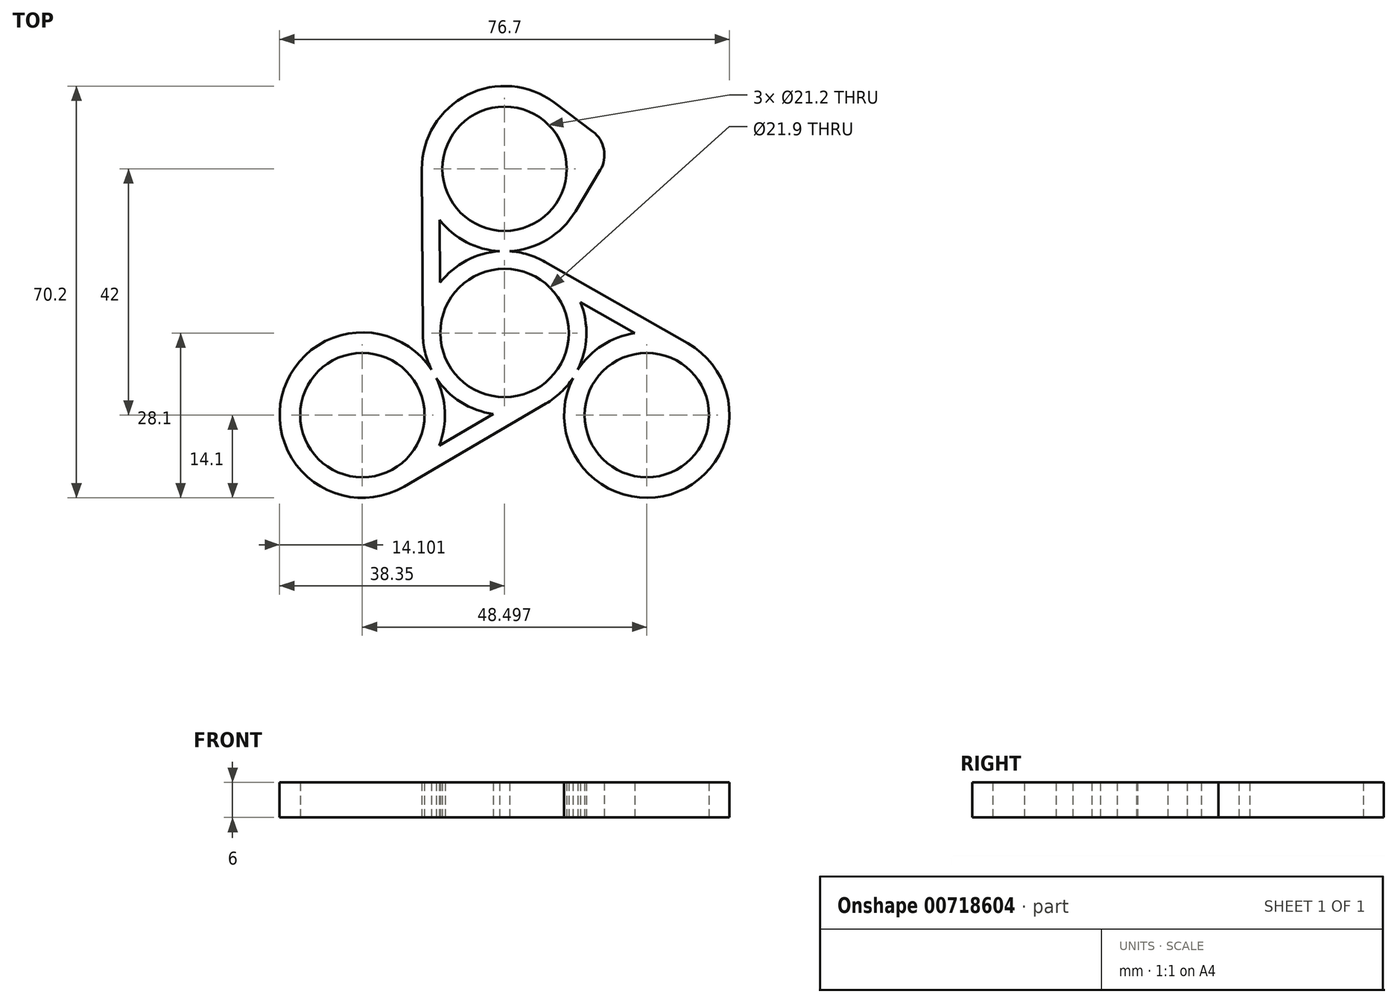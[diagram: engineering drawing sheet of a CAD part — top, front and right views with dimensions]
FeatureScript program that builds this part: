
annotation { "Feature Type Name" : "Feature", "Feature Type Description" : "" }
export const myFeature = defineFeature(function(context is Context, id is Id, definition is map)
    precondition{}
    {
        {
            var Q0;
            Q0=qCreatedBy(makeId("Top.planeOp"),FACE);
            var sketch = newSketch(context, id + "F0", { "sketchPlane" : qUnion([Q0])});
            skCircle(sketch, "E0", {"center": v(0, 0) * mm, "radius": 10.95 * mm});
            skCircle(sketch, "E1.cCircle", {"center": v(0, 0) * mm, "radius": 14 * mm, "construction": true});
            skLineSegment(sketch, "E1.0", {"start": v(0, 28) * mm, "end": v(24.25, -14) * mm, "construction": true});
            skLineSegment(sketch, "E1.1", {"start": v(24.25, -14) * mm, "end": v(-24.25, -14) * mm, "construction": true});
            skLineSegment(sketch, "E1.2", {"start": v(-24.25, -14) * mm, "end": v(0, 28) * mm, "construction": true});
            skPoint(sketch, "E1.0.midPoint", {"position": v(12.12, 7) * mm});
            skCircle(sketch, "E2", {"center": v(0, 28) * mm, "radius": 10.6 * mm});
            skCircle(sketch, "E3", {"center": v(24.25, -14) * mm, "radius": 10.6 * mm});
            skCircle(sketch, "E4", {"center": v(-24.25, -14) * mm, "radius": 10.6 * mm});
            skCircle(sketch, "E5.0", {"center": v(0, 0) * mm, "radius": 13.95 * mm});
            skCircle(sketch, "E6.0", {"center": v(0, 28) * mm, "radius": 14.1 * mm});
            skCircle(sketch, "E7.0", {"center": v(-24.25, -14) * mm, "radius": 14.1 * mm});
            skCircle(sketch, "E8.0", {"center": v(24.25, -14) * mm, "radius": 14.1 * mm});
            skLineSegment(sketch, "E9", {"start": v(-14.1, 27.92) * mm, "end": v(-13.95, -0.07) * mm});
            skLineSegment(sketch, "E10", {"start": v(7.04, -12.04) * mm, "end": v(-17.13, -26.17) * mm});
            skLineSegment(sketch, "E11", {"start": v(31.23, -1.75) * mm, "end": v(6.91, 12.12) * mm});
            skLineSegment(sketch, "E12.0", {"start": v(-11.1, 28.86) * mm, "end": v(-10.96, 0.91) * mm});
            skLineSegment(sketch, "E13.0", {"start": v(4.69, -9.94) * mm, "end": v(-19.44, -24.05) * mm});
            skLineSegment(sketch, "E14.0", {"start": v(30.54, -4.81) * mm, "end": v(6.27, 9.03) * mm});
            skLineSegment(sketch, "E15", {"start": v(6.91, 12.12) * mm, "end": v(6.94, 12.16) * mm});
            skLineSegment(sketch, "E16.trimOffspring", {"start": v(12.09, 20.74) * mm, "end": v(18.64, 31.65) * mm});
            skPoint(sketch, "E17.start.orphan", {"position": v(0, 42.1) * mm});
            skLineSegment(sketch, "E18", {"start": v(8.46, 39.28) * mm, "end": v(18.64, 31.65) * mm});
            skPoint(sketch, "E19.orphan", {"position": v(25.18, 42.55) * mm});
            skSolve(sketch);
        }
        {
            var Q0;
            Q0 = qSketchRegion(id + "F0", true);
            extrude(context, id + "F1", {"entities" : qUnion([Q0]), "depth" : 6 * mm, "offsetDistance" : 25 * mm});
        }
        {
            var Q0;
            Q0=makeQuery(id+"F1.opExtrude","SWEPT_EDGE",EDGE,{"disambiguationData":[OSD([sQuery(id+"F0.wireOp",EDGE,"E16.trimOffspring"),sQuery(id+"F0.wireOp",EDGE,"E18")])]});
            fillet(context, id + "F2", {"entities" : qUnion([Q0]), "radius" : 5 * mm, "tangentPropagation" : true, "allowEdgeOverflow" : false});
        }
    });
